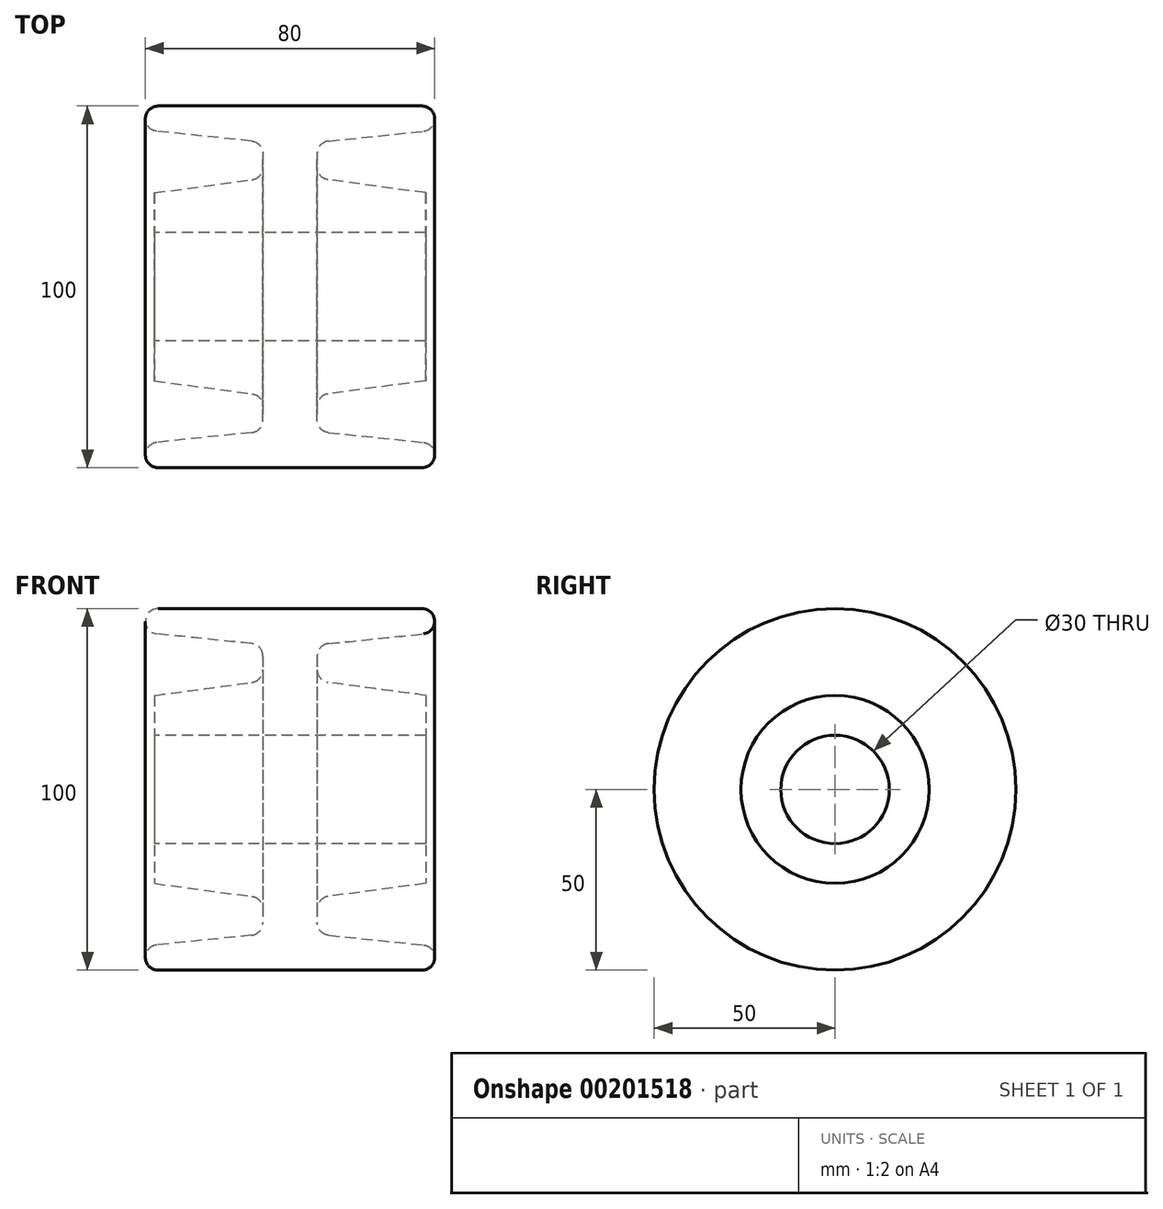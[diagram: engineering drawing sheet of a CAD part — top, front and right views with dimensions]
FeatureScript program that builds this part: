
annotation { "Feature Type Name" : "Feature", "Feature Type Description" : "" }
export const myFeature = defineFeature(function(context is Context, id is Id, definition is map)
    precondition{}
    {
        {
            var Q0;
            Q0=qCreatedBy(makeId("Top.planeOp"),FACE);
            var sketch = newSketch(context, id + "F0", { "sketchPlane" : qUnion([Q0])});
            skLineSegment(sketch, "E0", {"start": v(0, -15) * mm, "end": v(37.5, -15) * mm});
            skLineSegment(sketch, "E1", {"start": v(37.5, -15) * mm, "end": v(37.5, -26) * mm});
            skLineSegment(sketch, "E2", {"start": v(37.5, -26) * mm, "end": v(10.54, -29.6) * mm});
            skLineSegment(sketch, "E3", {"start": v(36.5, -50) * mm, "end": v(0, -50) * mm});
            skLineSegment(sketch, "E4", {"start": v(0, -50) * mm, "end": v(0, -15) * mm});
            skCircle(sketch, "E5", {"center": v(36.5, -46.5) * mm, "radius": 3.5 * mm});
            skLineSegment(sketch, "E6", {"start": v(36.86, -43.02) * mm, "end": v(10.64, -40.32) * mm});
            skLineSegment(sketch, "E7", {"start": v(7.5, -36.84) * mm, "end": v(7.5, -33.06) * mm});
            skPoint(sketch, "E8.visualSharp", {"position": v(7.5, -40) * mm});
            skArc(sketch, "E8.filletArc", {"start": v(7.5, -36.84) * mm, "mid": v(8.4, -39.19) * mm, "end": v(10.64, -40.32) * mm});
            skPoint(sketch, "E9.visualSharp", {"position": v(7.5, -30) * mm});
            skArc(sketch, "E9.filletArc", {"start": v(10.54, -29.6) * mm, "mid": v(8.37, -30.76) * mm, "end": v(7.5, -33.06) * mm});
            skLineSegment(sketch, "E10.MirrorCS", {"start": v(0, -15) * mm, "end": v(-37.5, -15) * mm});
            skLineSegment(sketch, "E11.MirrorCS", {"start": v(-37.5, -15) * mm, "end": v(-37.5, -26) * mm});
            skLineSegment(sketch, "E12.MirrorCS", {"start": v(-37.5, -26) * mm, "end": v(-10.54, -29.6) * mm});
            skArc(sketch, "E13.MirrorCS", {"start": v(-10.54, -29.6) * mm, "mid": v(-8.37, -30.76) * mm, "end": v(-7.5, -33.06) * mm});
            skLineSegment(sketch, "E14.MirrorCS", {"start": v(-7.5, -36.84) * mm, "end": v(-7.5, -33.06) * mm});
            skArc(sketch, "E15.MirrorCS", {"start": v(-7.5, -36.84) * mm, "mid": v(-8.4, -39.19) * mm, "end": v(-10.64, -40.32) * mm});
            skLineSegment(sketch, "E16.MirrorCS", {"start": v(-36.86, -43.02) * mm, "end": v(-10.64, -40.32) * mm});
            skCircle(sketch, "E17.MirrorC", {"center": v(-36.5, -46.5) * mm, "radius": 3.5 * mm});
            skLineSegment(sketch, "E18.MirrorCS", {"start": v(-36.5, -50) * mm, "end": v(0, -50) * mm});
            skLineSegment(sketch, "E19", {"start": v(-52.41, 0) * mm, "end": v(79.55, 0) * mm, "construction": true});
            skSolve(sketch);
        }
        {
            var Q0;
            Q0=qSketchRegion(id+"F0",true);
            var Q1;
            Q1=sQuery(id+"F0.wireOp",EDGE,"E19");
            revolve(context, id + "F1", {"entities" : qUnion([Q0]), "axis" : qUnion([Q1]), "revolveType" : RevolveType.FULL});
        }
    });
